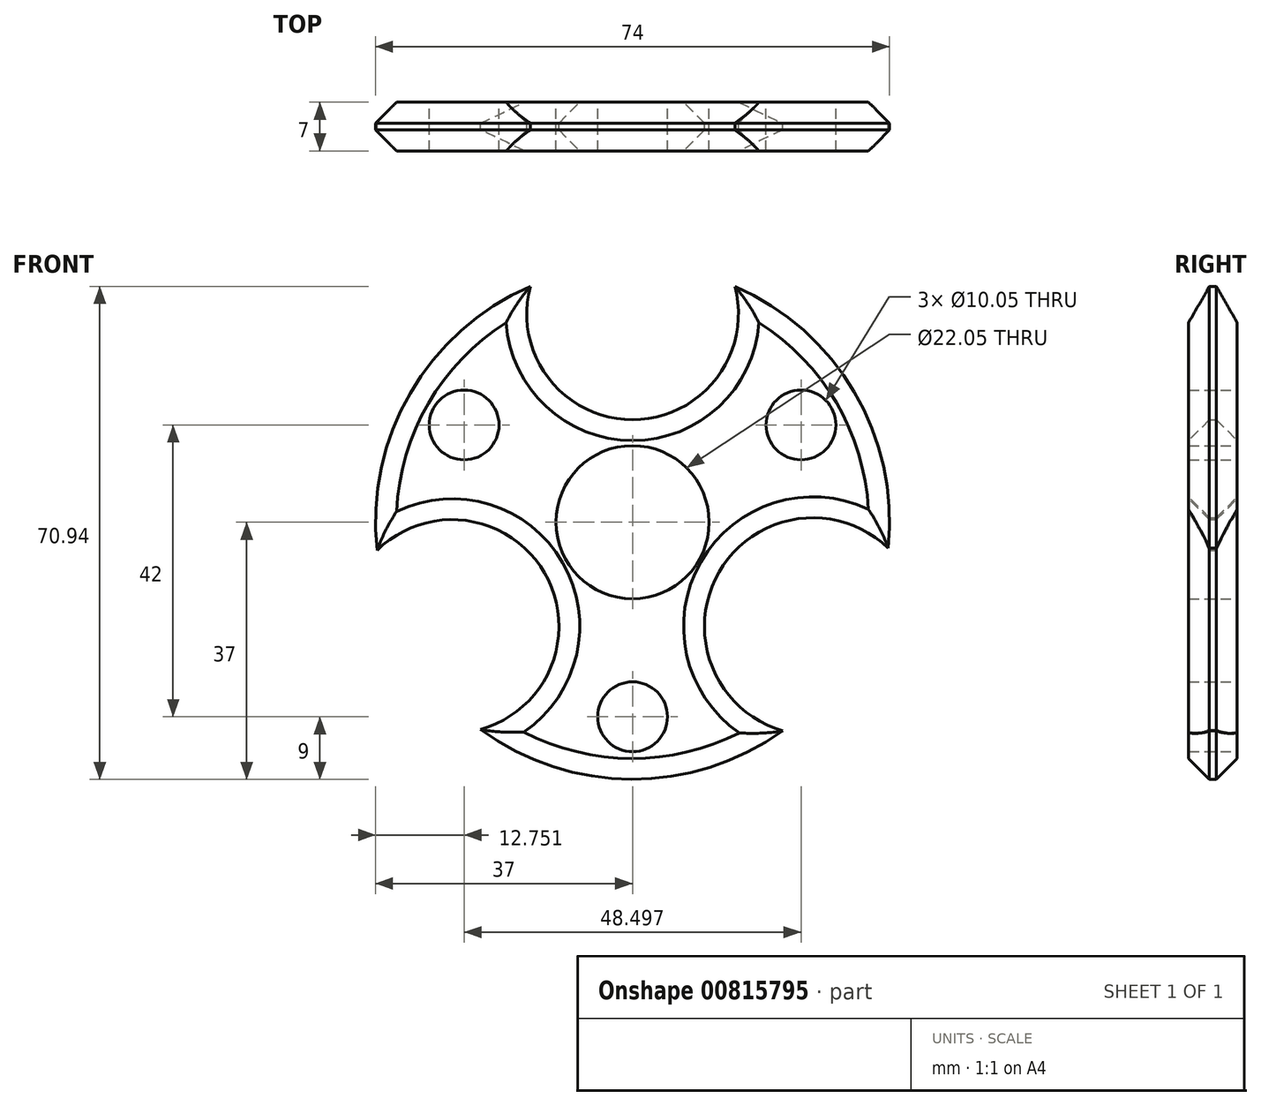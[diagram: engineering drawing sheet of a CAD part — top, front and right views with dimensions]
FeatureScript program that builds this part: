
annotation { "Feature Type Name" : "Feature", "Feature Type Description" : "" }
export const myFeature = defineFeature(function(context is Context, id is Id, definition is map)
    precondition{}
    {
        {
            var Q0;
            Q0=qCreatedBy(makeId("Front.planeOp"),FACE);
            var sketch = newSketch(context, id + "F0", { "sketchPlane" : qUnion([Q0])});
            skCircle(sketch, "E0", {"center": v(0, 0) * mm, "radius": 37 * mm});
            skCircle(sketch, "E1", {"center": v(0, 0) * mm, "radius": 11.03 * mm});
            skCircle(sketch, "E2", {"center": v(0, 0) * mm, "radius": 30 * mm});
            skCircle(sketch, "E3", {"center": v(0, 30) * mm, "radius": 15.25 * mm});
            skCircle(sketch, "E4", {"center": v(-25.98, -15) * mm, "radius": 15.37 * mm});
            skCircle(sketch, "E5", {"center": v(25.98, -15) * mm, "radius": 15.64 * mm});
            skLineSegment(sketch, "E6", {"start": v(0, 0) * mm, "end": v(-25.98, -15) * mm});
            skLineSegment(sketch, "E7", {"start": v(0, 0) * mm, "end": v(25.98, -15) * mm});
            skLineSegment(sketch, "E8", {"start": v(0, 0) * mm, "end": v(0, 30) * mm});
            skLineSegment(sketch, "E9", {"start": v(0, 0) * mm, "end": v(-32.04, 18.5) * mm});
            skLineSegment(sketch, "E10", {"start": v(0, 0) * mm, "end": v(0, -37) * mm});
            skLineSegment(sketch, "E11", {"start": v(0, 0) * mm, "end": v(32.04, 18.5) * mm});
            skCircle(sketch, "E12", {"center": v(-24.25, 14) * mm, "radius": 5.03 * mm});
            skCircle(sketch, "E13", {"center": v(24.25, 14) * mm, "radius": 5.03 * mm});
            skCircle(sketch, "E14", {"center": v(0, -28) * mm, "radius": 5.03 * mm});
            skSolve(sketch);
        }
        {
            var Q0;
            {var subQ0=sQuery(id+"F0.wireOp",EDGE,"E9");var subQ1=sQuery(id+"F0.wireOp",EDGE,"E0");var subQ2=makeQuery(id+"F0.imprint","INTERSECT",VERTEX,{"derivedFrom":[subQ1,subQ0]});Q0=makeQuery(id+"F0.imprint","IMPRINT",FACE,{"disambiguationData":[TD([[makeQuery(id+"F0.imprint","IMPRINT",EDGE,{"disambiguationData":[TD([[subQ2,-1.0]])],"derivedFrom":subQ1}),1.0]])]});}
            var Q1;
            {var subQ5=sQuery(id+"F0.wireOp",EDGE,"E1");var subQ9=sQuery(id+"F0.wireOp",EDGE,"E9");var subQ10=makeQuery(id+"F0.imprint","INTERSECT",VERTEX,{"derivedFrom":[subQ5,subQ9]});Q1=makeQuery(id+"F0.imprint","IMPRINT",FACE,{"disambiguationData":[TD([[makeQuery(id+"F0.imprint","IMPRINT",EDGE,{"disambiguationData":[TD([[subQ10,-1.0]])],"derivedFrom":subQ5}),-1.0]])]});}
            var Q2;
            {var subQ5=sQuery(id+"F0.wireOp",EDGE,"E8");var subQ6=sQuery(id+"F0.wireOp",EDGE,"E1");var subQ7=makeQuery(id+"F0.imprint","INTERSECT",VERTEX,{"derivedFrom":[subQ6,subQ5]});Q2=makeQuery(id+"F0.imprint","IMPRINT",FACE,{"disambiguationData":[TD([[makeQuery(id+"F0.imprint","IMPRINT",EDGE,{"disambiguationData":[TD([[subQ7,-1.0]])],"derivedFrom":subQ6}),-1.0]])]});}
            var Q3;
            {var subQ1=sQuery(id+"F0.wireOp",EDGE,"E0");var subQ5=sQuery(id+"F0.wireOp",EDGE,"E9");var subQ6=makeQuery(id+"F0.imprint","INTERSECT",VERTEX,{"derivedFrom":[subQ1,subQ5]});Q3=makeQuery(id+"F0.imprint","IMPRINT",FACE,{"disambiguationData":[TD([[makeQuery(id+"F0.imprint","IMPRINT",EDGE,{"disambiguationData":[TD([[subQ6,1.0]])],"derivedFrom":subQ1}),1.0]])]});}
            var Q4;
            {var subQ0=sQuery(id+"F0.wireOp",EDGE,"E8");var subQ1=sQuery(id+"F0.wireOp",EDGE,"E1");var subQ2=makeQuery(id+"F0.imprint","INTERSECT",VERTEX,{"derivedFrom":[subQ1,subQ0]});Q4=makeQuery(id+"F0.imprint","IMPRINT",FACE,{"disambiguationData":[TD([[makeQuery(id+"F0.imprint","IMPRINT",EDGE,{"disambiguationData":[TD([[subQ2,1.0]])],"derivedFrom":subQ1}),-1.0]])]});}
            var Q5;
            {var subQ0=sQuery(id+"F0.wireOp",EDGE,"E11");var subQ1=sQuery(id+"F0.wireOp",EDGE,"E0");var subQ2=makeQuery(id+"F0.imprint","INTERSECT",VERTEX,{"derivedFrom":[subQ1,subQ0]});Q5=makeQuery(id+"F0.imprint","IMPRINT",FACE,{"disambiguationData":[TD([[makeQuery(id+"F0.imprint","IMPRINT",EDGE,{"disambiguationData":[TD([[subQ2,-1.0]])],"derivedFrom":subQ1}),1.0]])]});}
            var Q6;
            {var subQ0=sQuery(id+"F0.wireOp",EDGE,"E11");var subQ1=sQuery(id+"F0.wireOp",EDGE,"E0");var subQ2=makeQuery(id+"F0.imprint","INTERSECT",VERTEX,{"derivedFrom":[subQ1,subQ0]});Q6=makeQuery(id+"F0.imprint","IMPRINT",FACE,{"disambiguationData":[TD([[makeQuery(id+"F0.imprint","IMPRINT",EDGE,{"disambiguationData":[TD([[subQ2,1.0]])],"derivedFrom":subQ1}),1.0]])]});}
            var Q7;
            {var subQ1=sQuery(id+"F0.wireOp",EDGE,"E1");var subQ9=sQuery(id+"F0.wireOp",EDGE,"E11");var subQ10=makeQuery(id+"F0.imprint","INTERSECT",VERTEX,{"derivedFrom":[subQ1,subQ9]});Q7=makeQuery(id+"F0.imprint","IMPRINT",FACE,{"disambiguationData":[TD([[makeQuery(id+"F0.imprint","IMPRINT",EDGE,{"disambiguationData":[TD([[subQ10,1.0]])],"derivedFrom":subQ1}),-1.0]])]});}
            var Q8;
            {var subQ1=sQuery(id+"F0.wireOp",EDGE,"E1");var subQ9=sQuery(id+"F0.wireOp",EDGE,"E10");var subQ10=makeQuery(id+"F0.imprint","INTERSECT",VERTEX,{"derivedFrom":[subQ1,subQ9]});Q8=makeQuery(id+"F0.imprint","IMPRINT",FACE,{"disambiguationData":[TD([[makeQuery(id+"F0.imprint","IMPRINT",EDGE,{"disambiguationData":[TD([[subQ10,-1.0]])],"derivedFrom":subQ1}),-1.0]])]});}
            var Q9;
            {var subQ0=sQuery(id+"F0.wireOp",EDGE,"E6");var subQ1=sQuery(id+"F0.wireOp",EDGE,"E1");var subQ2=makeQuery(id+"F0.imprint","INTERSECT",VERTEX,{"derivedFrom":[subQ1,subQ0]});Q9=makeQuery(id+"F0.imprint","IMPRINT",FACE,{"disambiguationData":[TD([[makeQuery(id+"F0.imprint","IMPRINT",EDGE,{"disambiguationData":[TD([[subQ2,-1.0]])],"derivedFrom":subQ1}),-1.0]])]});}
            var Q10;
            {var subQ0=sQuery(id+"F0.wireOp",EDGE,"E10");var subQ1=sQuery(id+"F0.wireOp",EDGE,"E0");var subQ2=makeQuery(id+"F0.imprint","INTERSECT",VERTEX,{"derivedFrom":[subQ1,subQ0]});Q10=makeQuery(id+"F0.imprint","IMPRINT",FACE,{"disambiguationData":[TD([[makeQuery(id+"F0.imprint","IMPRINT",EDGE,{"disambiguationData":[TD([[subQ2,1.0]])],"derivedFrom":subQ1}),1.0]])]});}
            var Q11;
            {var subQ5=sQuery(id+"F0.wireOp",EDGE,"E10");var subQ6=sQuery(id+"F0.wireOp",EDGE,"E0");var subQ7=makeQuery(id+"F0.imprint","INTERSECT",VERTEX,{"derivedFrom":[subQ6,subQ5]});Q11=makeQuery(id+"F0.imprint","IMPRINT",FACE,{"disambiguationData":[TD([[makeQuery(id+"F0.imprint","IMPRINT",EDGE,{"disambiguationData":[TD([[subQ7,-1.0]])],"derivedFrom":subQ6}),1.0]])]});}
            extrude(context, id + "F1", {"entities" : qUnion([Q0, Q1, Q2, Q3, Q4, Q5, Q6, Q7, Q8, Q9, Q10, Q11]), "depth" : 7 * mm, "offsetDistance" : 25 * mm});
        }
        {
            var Q0;
            {var subQ0=sQuery(id+"F0.wireOp",EDGE,"E0");var subQ1=makeQuery(id+"F0.imprint","INTERSECT",VERTEX,{"derivedFrom":[subQ0,sQuery(id+"F0.wireOp",EDGE,"E9")]});Q0=makeQuery(id+"F1.opExtrude","CAP_EDGE",EDGE,{"disambiguationData":[OSD([subQ0]),TDD([makeQuery(id+"F0.imprint","IMPRINT",EDGE,{"disambiguationData":[TD([[subQ1,1.0]])],"derivedFrom":subQ0}),makeQuery(id+"F0.imprint","IMPRINT",EDGE,{"disambiguationData":[TD([[subQ1,-1.0]])],"derivedFrom":subQ0})])],"isStart":false});}
            var Q1;
            Q1=makeQuery(id+"F1.opExtrude","CAP_EDGE",EDGE,{"disambiguationData":[OSD([sQuery(id+"F0.wireOp",EDGE,"E4")])],"isStart":false});
            var Q2;
            {var subQ0=sQuery(id+"F0.wireOp",EDGE,"E0");var subQ1=makeQuery(id+"F0.imprint","INTERSECT",VERTEX,{"derivedFrom":[subQ0,sQuery(id+"F0.wireOp",EDGE,"E10")]});Q2=makeQuery(id+"F1.opExtrude","CAP_EDGE",EDGE,{"disambiguationData":[OSD([subQ0]),TDD([makeQuery(id+"F0.imprint","IMPRINT",EDGE,{"disambiguationData":[TD([[subQ1,1.0]])],"derivedFrom":subQ0}),makeQuery(id+"F0.imprint","IMPRINT",EDGE,{"disambiguationData":[TD([[subQ1,-1.0]])],"derivedFrom":subQ0})])],"isStart":false});}
            var Q3;
            Q3=makeQuery(id+"F1.opExtrude","CAP_EDGE",EDGE,{"disambiguationData":[OSD([sQuery(id+"F0.wireOp",EDGE,"E5")])],"isStart":false});
            var Q4;
            Q4=makeQuery(id+"F1.opExtrude","CAP_EDGE",EDGE,{"disambiguationData":[OSD([sQuery(id+"F0.wireOp",EDGE,"E3")])],"isStart":false});
            var Q5;
            {var subQ0=sQuery(id+"F0.wireOp",EDGE,"E0");var subQ1=makeQuery(id+"F0.imprint","INTERSECT",VERTEX,{"derivedFrom":[subQ0,sQuery(id+"F0.wireOp",EDGE,"E11")]});Q5=makeQuery(id+"F1.opExtrude","CAP_EDGE",EDGE,{"disambiguationData":[OSD([subQ0]),TDD([makeQuery(id+"F0.imprint","IMPRINT",EDGE,{"disambiguationData":[TD([[subQ1,-1.0]])],"derivedFrom":subQ0}),makeQuery(id+"F0.imprint","IMPRINT",EDGE,{"disambiguationData":[TD([[subQ1,1.0]])],"derivedFrom":subQ0})])],"isStart":false});}
            var Q6;
            {var subQ0=sQuery(id+"F0.wireOp",EDGE,"E0");var subQ1=makeQuery(id+"F0.imprint","INTERSECT",VERTEX,{"derivedFrom":[subQ0,sQuery(id+"F0.wireOp",EDGE,"E11")]});Q6=makeQuery(id+"F1.opExtrude","CAP_EDGE",EDGE,{"disambiguationData":[OSD([subQ0]),TDD([makeQuery(id+"F0.imprint","IMPRINT",EDGE,{"disambiguationData":[TD([[subQ1,-1.0]])],"derivedFrom":subQ0}),makeQuery(id+"F0.imprint","IMPRINT",EDGE,{"disambiguationData":[TD([[subQ1,1.0]])],"derivedFrom":subQ0})])],"isStart":true});}
            var Q7;
            Q7=makeQuery(id+"F1.opExtrude","CAP_EDGE",EDGE,{"disambiguationData":[OSD([sQuery(id+"F0.wireOp",EDGE,"E5")])],"isStart":true});
            var Q8;
            {var subQ0=sQuery(id+"F0.wireOp",EDGE,"E0");var subQ1=makeQuery(id+"F0.imprint","INTERSECT",VERTEX,{"derivedFrom":[subQ0,sQuery(id+"F0.wireOp",EDGE,"E10")]});Q8=makeQuery(id+"F1.opExtrude","CAP_EDGE",EDGE,{"disambiguationData":[OSD([subQ0]),TDD([makeQuery(id+"F0.imprint","IMPRINT",EDGE,{"disambiguationData":[TD([[subQ1,1.0]])],"derivedFrom":subQ0}),makeQuery(id+"F0.imprint","IMPRINT",EDGE,{"disambiguationData":[TD([[subQ1,-1.0]])],"derivedFrom":subQ0})])],"isStart":true});}
            var Q9;
            Q9=makeQuery(id+"F1.opExtrude","CAP_EDGE",EDGE,{"disambiguationData":[OSD([sQuery(id+"F0.wireOp",EDGE,"E4")])],"isStart":true});
            var Q10;
            {var subQ0=sQuery(id+"F0.wireOp",EDGE,"E0");var subQ1=makeQuery(id+"F0.imprint","INTERSECT",VERTEX,{"derivedFrom":[subQ0,sQuery(id+"F0.wireOp",EDGE,"E9")]});Q10=makeQuery(id+"F1.opExtrude","CAP_EDGE",EDGE,{"disambiguationData":[OSD([subQ0]),TDD([makeQuery(id+"F0.imprint","IMPRINT",EDGE,{"disambiguationData":[TD([[subQ1,1.0]])],"derivedFrom":subQ0}),makeQuery(id+"F0.imprint","IMPRINT",EDGE,{"disambiguationData":[TD([[subQ1,-1.0]])],"derivedFrom":subQ0})])],"isStart":true});}
            var Q11;
            Q11=makeQuery(id+"F1.opExtrude","CAP_EDGE",EDGE,{"disambiguationData":[OSD([sQuery(id+"F0.wireOp",EDGE,"E3")])],"isStart":true});
            chamfer(context, id + "F2", {"entities" : qUnion([Q0, Q1, Q2, Q3, Q4, Q5, Q6, Q7, Q8, Q9, Q10, Q11]), "width" : 3 * mm, "tangentPropagation" : true});
        }
    });
